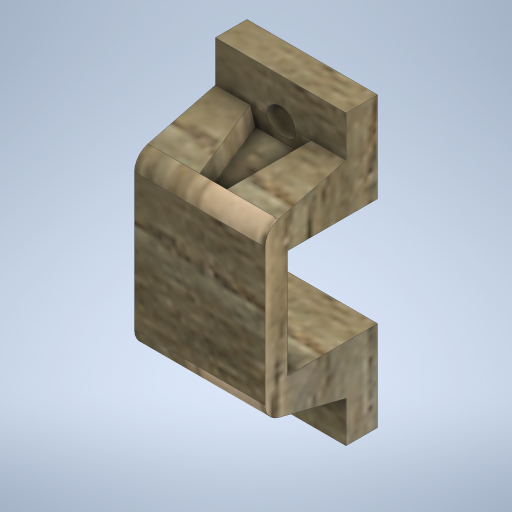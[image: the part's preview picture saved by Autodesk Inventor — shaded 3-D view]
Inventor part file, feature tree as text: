
AUTODESK INVENTOR PART (.ipt)
format: ipt  version: 2024 (Build 280153020, 153B)  size: 450,048 bytes
history: native  units: mm
features: extrude x5, sketch x5
ambient origin geometry x8: Origin, YZ Plane, XZ Plane, XY Plane, X Axis, Y Axis, Z Axis, Center Point
bodies: Solid1 (feature_tree)
feature tree (10):
  extrude  "Extrusion1"  Depth=10.0mm
  extrude  "Extrusion2"  Depth=10.0mm
  extrude  "Extrusion3"  Depth=3.5mm
  extrude  "Extrusion4"  Depth=14.5mm TaperAngle=0.0deg
  extrude  "Extrusion5"  Depth=2.5mm
  sketch  "Sketch1"  dims[d0=12.0mm d1=10.0mm]
  sketch  "Sketch2"  dims[d2=2.5mm d3=10.0mm]
  sketch  "Sketch3"  dims[d4=3.5mm d5=4.56mm]
  sketch  "Sketch4"  dims[d6=2.0mm d7=14.5mm d8=0.0mm]
  sketch  "Sketch5"  dims[d13=1.5mm d14=1.5mm d15=3.4mm d16=3.4mm d17=2.5mm d18=0.0mm d19=3.2mm d20=4.0mm d21=0.0mm d22=3.4mm d23=3.4mm d25=1.5mm d26=1.5mm d27=2.5mm d28=0.0mm d29=3.2mm d30=4.0mm d31=0.0mm]
